# Revit family: 351_36364
name_source: partatom
category: Plumbing Fixtures
units: mm (PartAtom-declared; Revit-internal decimal feet)

## family parameters
Always vertical = Yes
Cut with Voids When Loaded = No
Part Type = Normal
Room Calculation Point = No
Round Connector Dimension = Use Diameter
Shared = No
Work Plane-Based = No

## types (1)
- 5650129 IDO GLOW WC-ISTUIN
    CAT0 = Yes
    CLBTZ = 0 mm  [stored 0 ft]
    CL_Location_5000 = 5000 mm  [stored 16.4042 ft]
    DC = 110 mm
    Description = WC GLOW universal model, slow close seat
    H1 = 420 mm  [stored 1.37795 ft]
    H2 = 430 mm
    H3 = 180 mm  [stored 0.590551 ft]
    H4 = 300 mm  [stored 0.984252 ft]
    H5 = 370 mm  [stored 1.21391 ft]
    L1 = 118 mm
    L2 = 124 mm  [stored 0.406824 ft]
    L3 = 153 mm  [stored 0.501969 ft]
    L4 = 178 mm
    QmdConnectorList = 601;DC
    URL = http://www.ido.fi
    W1 = 368 mm
    W2 = 402 mm  [stored 1.3189 ft]
    W3 = 446 mm  [stored 1.46325 ft]
    W4 = 473 mm
    XRefLineVPlnId = 7453
    YRefLineVPlnId = 7456
    magiPartTypeId = 351
    magiProductCode = 5650129 IDO GLOW WC-ISTUIN
    magiProductFamilyId = 36364
    magiProductId = 36364

note: [stored X ft] marks values corroborated as IEEE doubles in the binary element streams (Revit-internal decimal feet)

## geometry (parser evidence)
native form markers: Sweep x3
no freeform markers — native parametric forms only
